# Revit family: Controller TBOS-BT
name_source: partatom
category: Dispositivos de dados
units: mm (PartAtom-declared; Revit-internal decimal feet)

## family parameters
Com base no plano de trabalho = Não
Compartilhado = Não
Corte com vazios quando carregada = Não
Cota do conector redondo = Utilizar diâmetro
Manter orientação da anotação = Não
Número OmniClass = 23.85.50.00
Ponto de cálculo do ambiente = Não
Sempre na vertical = Sim
Tipo de parte = Normal
Título OmniClass = Communication Systems

## types (4) — shared parameters
Corrente de Saída = 2 A
DTT1 = 6
DTT2 = 2
DTT3 = 3
DTT4 = 3
DTT5 = 1
DTT7 = 2
DTT8 = 2
Heigth = 20
Length = 12
Plastic Black = Black
Plastic Blue = Blue
Power = 30 VA
RainBird: Code = F48504B
RainBird: Product Link = www.rainbird.com
Supply = 230 VA
SupportProjetos: Level of Detail = LOD 300
SupportProjetos: Review = R00
Tipo de imagem = <Nenhum>
URL = www.rainbird.com
Width = 4
zero-valued in all types: Elevação padrão, Heigth of TBOS

## type names (no varying parameters)
- TBOS-BT1
- TBOS-BT2
- TBOS-BT6
- TBOS-BT4

note: column(s) folded — value = type name in every type: Comentários de tipos, Modelo, RainBird: Description
